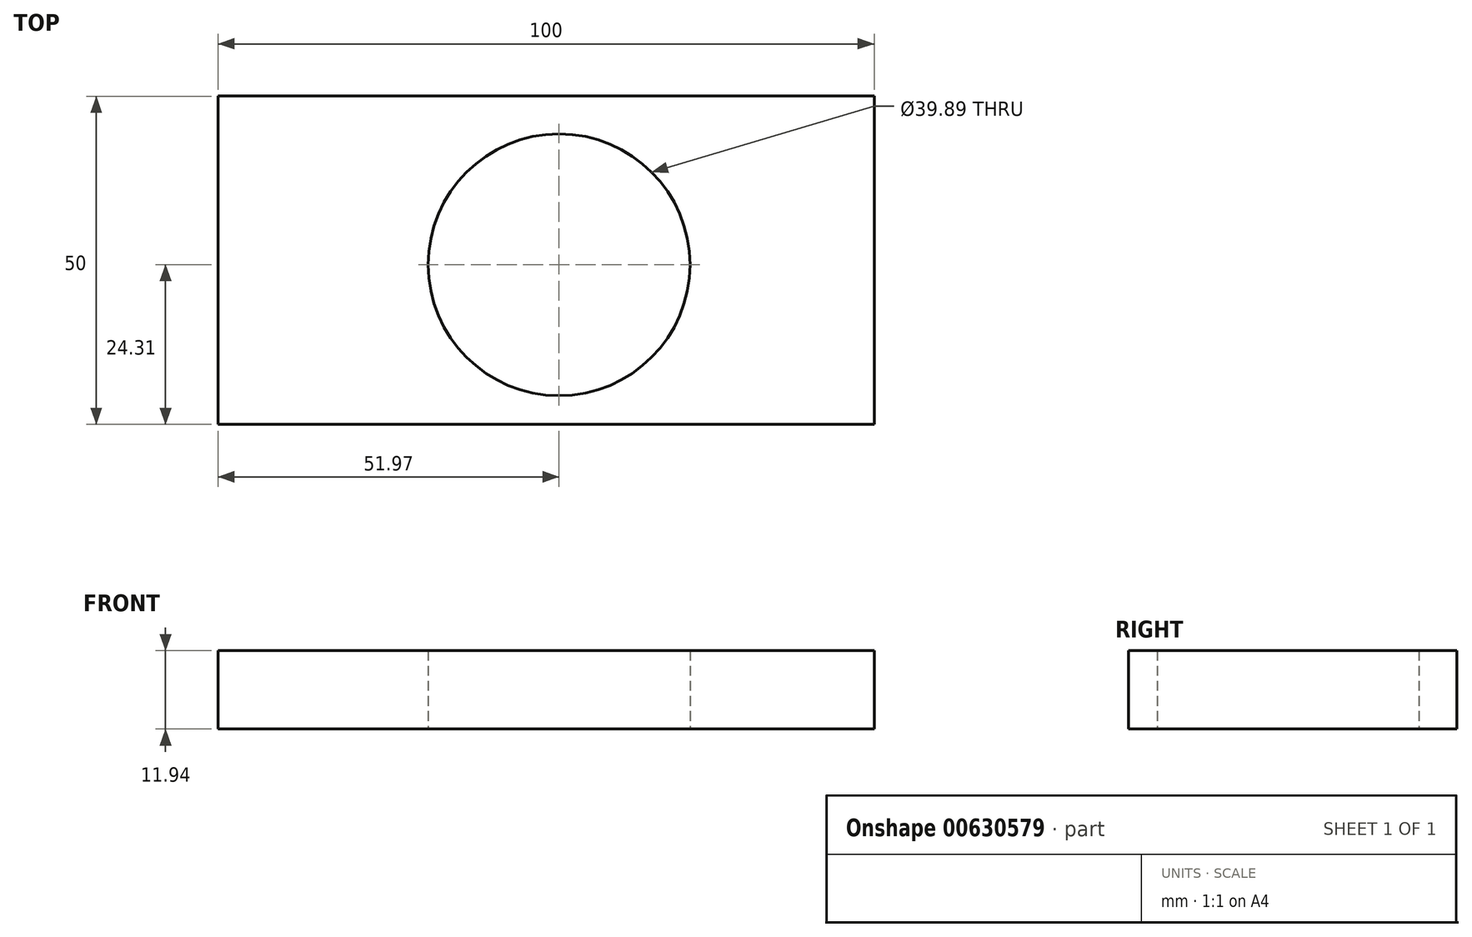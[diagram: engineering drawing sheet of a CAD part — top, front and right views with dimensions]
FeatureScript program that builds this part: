
annotation { "Feature Type Name" : "Feature", "Feature Type Description" : "" }
export const myFeature = defineFeature(function(context is Context, id is Id, definition is map)
    precondition{}
    {
        {
            var Q0;
            Q0=qCreatedBy(makeId("Top.planeOp"),FACE);
            var sketch = newSketch(context, id + "F0", { "sketchPlane" : qUnion([Q0])});
            skLineSegment(sketch, "E0.bottom", {"start": v(-51.97, 25.7) * mm, "end": v(48.03, 25.7) * mm});
            skLineSegment(sketch, "E0.top", {"start": v(-51.97, -24.3) * mm, "end": v(48.03, -24.3) * mm});
            skLineSegment(sketch, "E0.left", {"start": v(-51.97, 25.7) * mm, "end": v(-51.97, -24.3) * mm});
            skLineSegment(sketch, "E0.right", {"start": v(48.03, 25.7) * mm, "end": v(48.03, -24.3) * mm});
            skCircle(sketch, "E1", {"center": v(0, 0) * mm, "radius": 19.95 * mm});
            skSolve(sketch);
        }
        {
            var Q0;
            Q0=makeQuery(id+"F0.imprint","IMPRINT",FACE,{"disambiguationData":[TD([[makeQuery(id+"F0.imprint","IMPRINT",EDGE,{"derivedFrom":sQuery(id+"F0.wireOp",EDGE,"E0.bottom")}),-1.0]])]});
            extrude(context, id + "F1", {"entities" : qUnion([Q0]), "depth" : 11.94 * mm, "offsetDistance" : 25.4 * mm});
        }
    });
